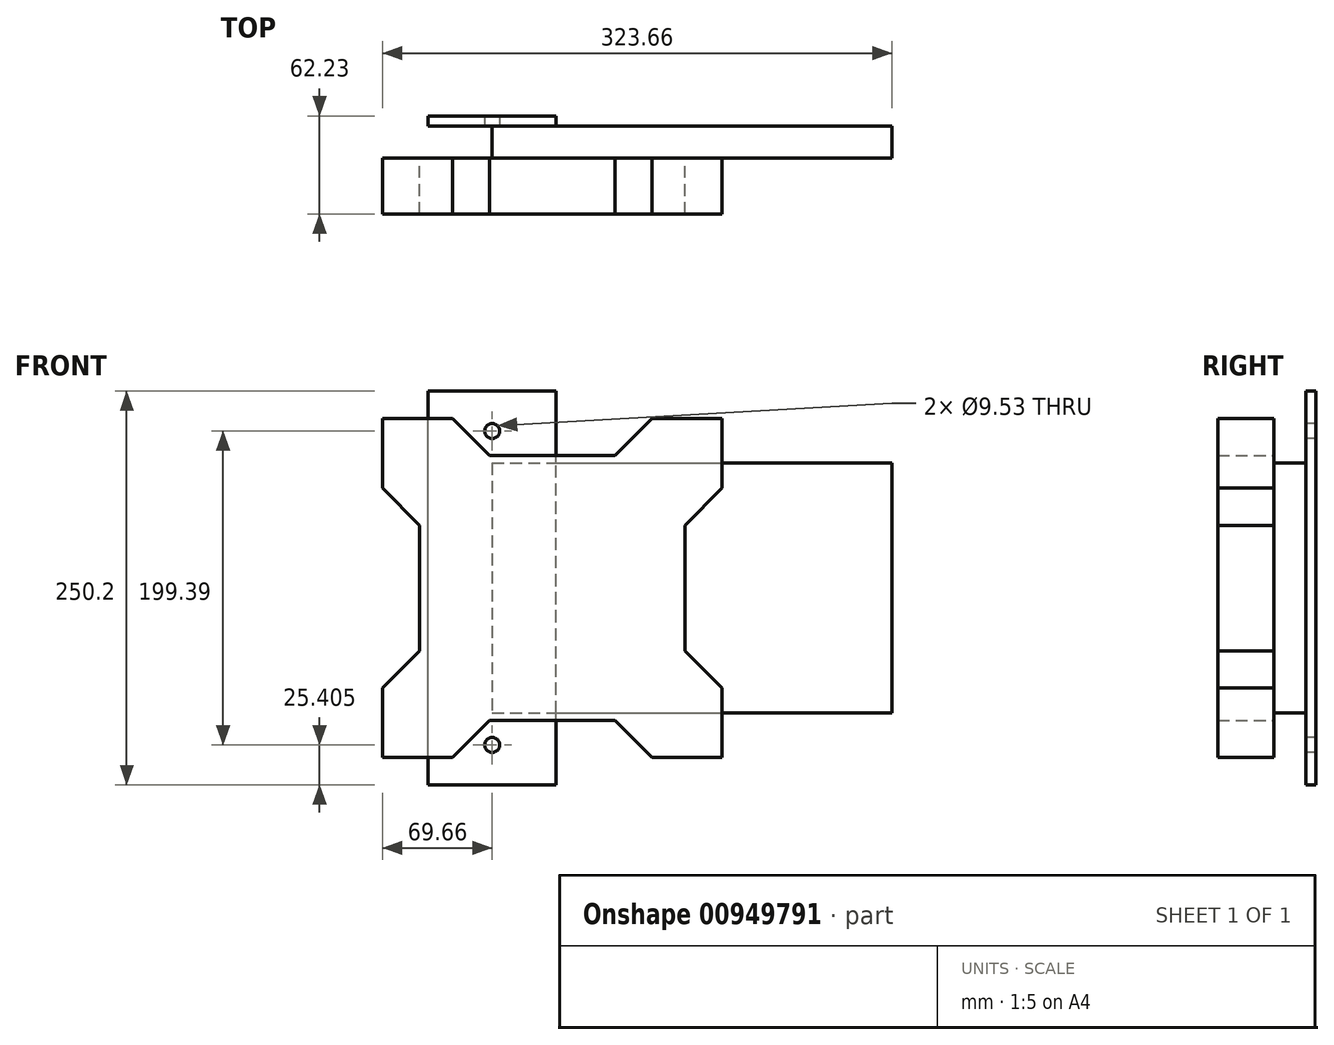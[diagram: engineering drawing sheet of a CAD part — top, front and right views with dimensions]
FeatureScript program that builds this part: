
annotation { "Feature Type Name" : "Feature", "Feature Type Description" : "" }
export const myFeature = defineFeature(function(context is Context, id is Id, definition is map)
    precondition{}
    {
        {
            var Q0;
            Q0=qCreatedBy(makeId("Front.planeOp"),FACE);
            var sketch = newSketch(context, id + "F0", { "sketchPlane" : qUnion([Q0])});
            skLineSegment(sketch, "E0", {"start": v(0, 0) * mm, "end": v(107.76, 107.76) * mm});
            skLineSegment(sketch, "E1", {"start": v(-362.28, 0) * mm, "end": v(475.85, 0) * mm, "construction": true});
            skLineSegment(sketch, "E2", {"start": v(0, 207.66) * mm, "end": v(0, -260.35) * mm, "construction": true});
            skLineSegment(sketch, "E3", {"start": v(107.76, 107.76) * mm, "end": v(63.4, 107.76) * mm});
            skLineSegment(sketch, "E4", {"start": v(63.4, 107.76) * mm, "end": v(39.86, 84.22) * mm});
            skLineSegment(sketch, "E5", {"start": v(39.86, 84.22) * mm, "end": v(0, 84.22) * mm});
            skLineSegment(sketch, "E6.MirrorCS", {"start": v(107.76, 107.76) * mm, "end": v(107.76, 63.4) * mm});
            skLineSegment(sketch, "E7.MirrorCS", {"start": v(84.22, 39.86) * mm, "end": v(84.22, 0) * mm});
            skLineSegment(sketch, "E8.MirrorCS", {"start": v(107.76, 63.4) * mm, "end": v(84.22, 39.86) * mm});
            skLineSegment(sketch, "E9.MirrorCS", {"start": v(-84.22, 39.86) * mm, "end": v(-84.22, 0) * mm});
            skLineSegment(sketch, "E10.MirrorCS", {"start": v(-107.76, 63.4) * mm, "end": v(-84.22, 39.86) * mm});
            skLineSegment(sketch, "E11.MirrorCS", {"start": v(-107.76, 107.76) * mm, "end": v(-107.76, 63.4) * mm});
            skLineSegment(sketch, "E12.MirrorCS", {"start": v(-107.76, 107.76) * mm, "end": v(-63.4, 107.76) * mm});
            skLineSegment(sketch, "E13.MirrorCS", {"start": v(-39.86, 84.22) * mm, "end": v(0, 84.22) * mm});
            skLineSegment(sketch, "E14.MirrorCS", {"start": v(-63.4, 107.76) * mm, "end": v(-39.86, 84.22) * mm});
            skLineSegment(sketch, "E15.MirrorCS", {"start": v(-107.76, -107.76) * mm, "end": v(-63.4, -107.76) * mm});
            skLineSegment(sketch, "E16.MirrorCS", {"start": v(39.86, -84.22) * mm, "end": v(0, -84.22) * mm});
            skLineSegment(sketch, "E17.MirrorCS", {"start": v(-107.76, -107.76) * mm, "end": v(-107.76, -63.4) * mm});
            skLineSegment(sketch, "E18.MirrorCS", {"start": v(-63.4, -107.76) * mm, "end": v(-39.86, -84.22) * mm});
            skLineSegment(sketch, "E19.MirrorCS", {"start": v(63.4, -107.76) * mm, "end": v(39.86, -84.22) * mm});
            skLineSegment(sketch, "E20.MirrorCS", {"start": v(-107.76, -63.4) * mm, "end": v(-84.22, -39.86) * mm});
            skLineSegment(sketch, "E21.MirrorCS", {"start": v(107.76, -63.4) * mm, "end": v(84.22, -39.86) * mm});
            skLineSegment(sketch, "E22.MirrorCS", {"start": v(107.76, -107.76) * mm, "end": v(63.4, -107.76) * mm});
            skLineSegment(sketch, "E23.MirrorCS", {"start": v(-39.86, -84.22) * mm, "end": v(0, -84.22) * mm});
            skLineSegment(sketch, "E24.MirrorCS", {"start": v(84.22, -39.86) * mm, "end": v(84.22, 0) * mm});
            skLineSegment(sketch, "E25.MirrorCS", {"start": v(-84.22, -39.86) * mm, "end": v(-84.22, 0) * mm});
            skLineSegment(sketch, "E26.MirrorCS", {"start": v(107.76, -107.76) * mm, "end": v(107.76, -63.4) * mm});
            skSolve(sketch);
        }
        {
            var Q0;
            Q0=makeQuery(id+"F0.imprint","IMPRINT",FACE,{"disambiguationData":[TD([[makeQuery(id+"F0.imprint","IMPRINT",EDGE,{"derivedFrom":sQuery(id+"F0.wireOp",EDGE,"E3")}),1.0]])]});
            extrude(context, id + "F1", {"entities" : qUnion([Q0]), "depth" : 35.56 * mm, "offsetDistance" : 25.4 * mm});
        }
        {
            var Q0;
            Q0=qCreatedBy(makeId("Front.planeOp"),FACE);
            var sketch = newSketch(context, id + "F2", { "sketchPlane" : qUnion([Q0])});
            skLineSegment(sketch, "E27.bottom", {"start": v(-38.1, 79.37) * mm, "end": v(215.9, 79.37) * mm});
            skLineSegment(sketch, "E27.top", {"start": v(-38.1, -79.37) * mm, "end": v(215.9, -79.38) * mm});
            skLineSegment(sketch, "E27.left", {"start": v(-38.1, 79.38) * mm, "end": v(-38.1, -79.38) * mm});
            skLineSegment(sketch, "E27.right", {"start": v(215.9, 79.38) * mm, "end": v(215.9, -79.37) * mm});
            skPoint(sketch, "E28", {"position": v(-38.1, 0) * mm});
            skSolve(sketch);
        }
        {
            var Q0;
            Q0 = qSketchRegion(id + "F2", true);
            extrude(context, id + "F3", {"entities" : qUnion([Q0]), "operationType" : NewBodyOperationType.ADD, "oppositeDirection" : true, "depth" : 20.32 * mm, "offsetDistance" : 25.4 * mm});
        }
        {
            var Q0;
            Q0=makeQuery(id+"F3.opExtrude","CAP_FACE",FACE,{"disambiguationData":[OSD([sQuery(id+"F2.wireOp",EDGE,"E27.bottom"),sQuery(id+"F2.wireOp",EDGE,"E27.top"),sQuery(id+"F2.wireOp",EDGE,"E27.left"),sQuery(id+"F2.wireOp",EDGE,"E27.right")])],"isStart":false});
            var sketch = newSketch(context, id + "F4", { "sketchPlane" : qUnion([Q0])});
            skLineSegment(sketch, "E29.bottom", {"start": v(78.74, -125.1) * mm, "end": v(-2.54, -125.1) * mm});
            skLineSegment(sketch, "E29.top", {"start": v(78.74, 125.1) * mm, "end": v(-2.54, 125.1) * mm});
            skLineSegment(sketch, "E29.left", {"start": v(78.74, -125.1) * mm, "end": v(78.74, 125.1) * mm});
            skLineSegment(sketch, "E29.right", {"start": v(-2.54, -125.1) * mm, "end": v(-2.54, 125.1) * mm});
            skLineSegment(sketch, "E30", {"start": v(38.1, 204.66) * mm, "end": v(38.1, -330.58) * mm, "construction": true});
            skPoint(sketch, "E30.startSnap0", {"position": v(38.1, 125.1) * mm});
            skPoint(sketch, "E31", {"position": v(38.1, 99.7) * mm});
            skPoint(sketch, "E32", {"position": v(38.1, -99.7) * mm});
            skSolve(sketch);
        }
        {
            var Q0;
            Q0 = qSketchRegion(id + "F4", true);
            extrude(context, id + "F5", {"entities" : qUnion([Q0]), "operationType" : NewBodyOperationType.ADD, "depth" : 6.35 * mm, "offsetDistance" : 25.4 * mm});
        }
        {
            var Q0;
            Q0=sQuery(id+"F4.wireOp",VERTEX,"E31");
            var Q1;
            Q1=sQuery(id+"F4.wireOp",VERTEX,"E32");
            var Q2;
            Q2=makeQuery(id+"F1.opExtrude","SWEPT_BODY",BODY,{"disambiguationData":[OSD([sQuery(id+"F0.wireOp",EDGE,"E3"),sQuery(id+"F0.wireOp",EDGE,"E4"),sQuery(id+"F0.wireOp",EDGE,"E5"),sQuery(id+"F0.wireOp",EDGE,"E6.MirrorCS"),sQuery(id+"F0.wireOp",EDGE,"E7.MirrorCS"),sQuery(id+"F0.wireOp",EDGE,"E8.MirrorCS"),sQuery(id+"F0.wireOp",EDGE,"E9.MirrorCS"),sQuery(id+"F0.wireOp",EDGE,"E10.MirrorCS"),sQuery(id+"F0.wireOp",EDGE,"E11.MirrorCS"),sQuery(id+"F0.wireOp",EDGE,"E12.MirrorCS"),sQuery(id+"F0.wireOp",EDGE,"E13.MirrorCS"),sQuery(id+"F0.wireOp",EDGE,"E14.MirrorCS"),sQuery(id+"F0.wireOp",EDGE,"E15.MirrorCS"),sQuery(id+"F0.wireOp",EDGE,"E16.MirrorCS"),sQuery(id+"F0.wireOp",EDGE,"E17.MirrorCS"),sQuery(id+"F0.wireOp",EDGE,"E18.MirrorCS"),sQuery(id+"F0.wireOp",EDGE,"E19.MirrorCS"),sQuery(id+"F0.wireOp",EDGE,"E20.MirrorCS"),sQuery(id+"F0.wireOp",EDGE,"E21.MirrorCS"),sQuery(id+"F0.wireOp",EDGE,"E22.MirrorCS"),sQuery(id+"F0.wireOp",EDGE,"E23.MirrorCS"),sQuery(id+"F0.wireOp",EDGE,"E24.MirrorCS"),sQuery(id+"F0.wireOp",EDGE,"E25.MirrorCS"),sQuery(id+"F0.wireOp",EDGE,"E26.MirrorCS")])]});
            hole(context, id + "F6", {"style" : HoleStyle.SIMPLE, "endStyle" : HoleEndStyle.THROUGH, "oppositeDirection" : true, "holeDiameter" : 9.52 * mm, "majorDiameter" : 6.35 * mm, "isTappedThrough" : true, "tappedDepth" : 12.7 * mm, "tapClearance" : 3, "startFromSketch" : true, "locations" : qUnion([Q0, Q1]), "scope" : qUnion([Q2])});
        }
        {
            var Q0;
            Q0=makeQuery(id+"F5.opExtrude","CAP_FACE",FACE,{"disambiguationData":[OSD([sQuery(id+"F4.wireOp",EDGE,"E29.bottom"),sQuery(id+"F4.wireOp",EDGE,"E29.top"),sQuery(id+"F4.wireOp",EDGE,"E29.left"),sQuery(id+"F4.wireOp",EDGE,"E29.right")])],"isStart":false});
            var sketch = newSketch(context, id + "F7", { "sketchPlane" : qUnion([Q0])});
            skPoint(sketch, "E33", {"position": v(0, 0) * mm});
            skSolve(sketch);
        }
    });
